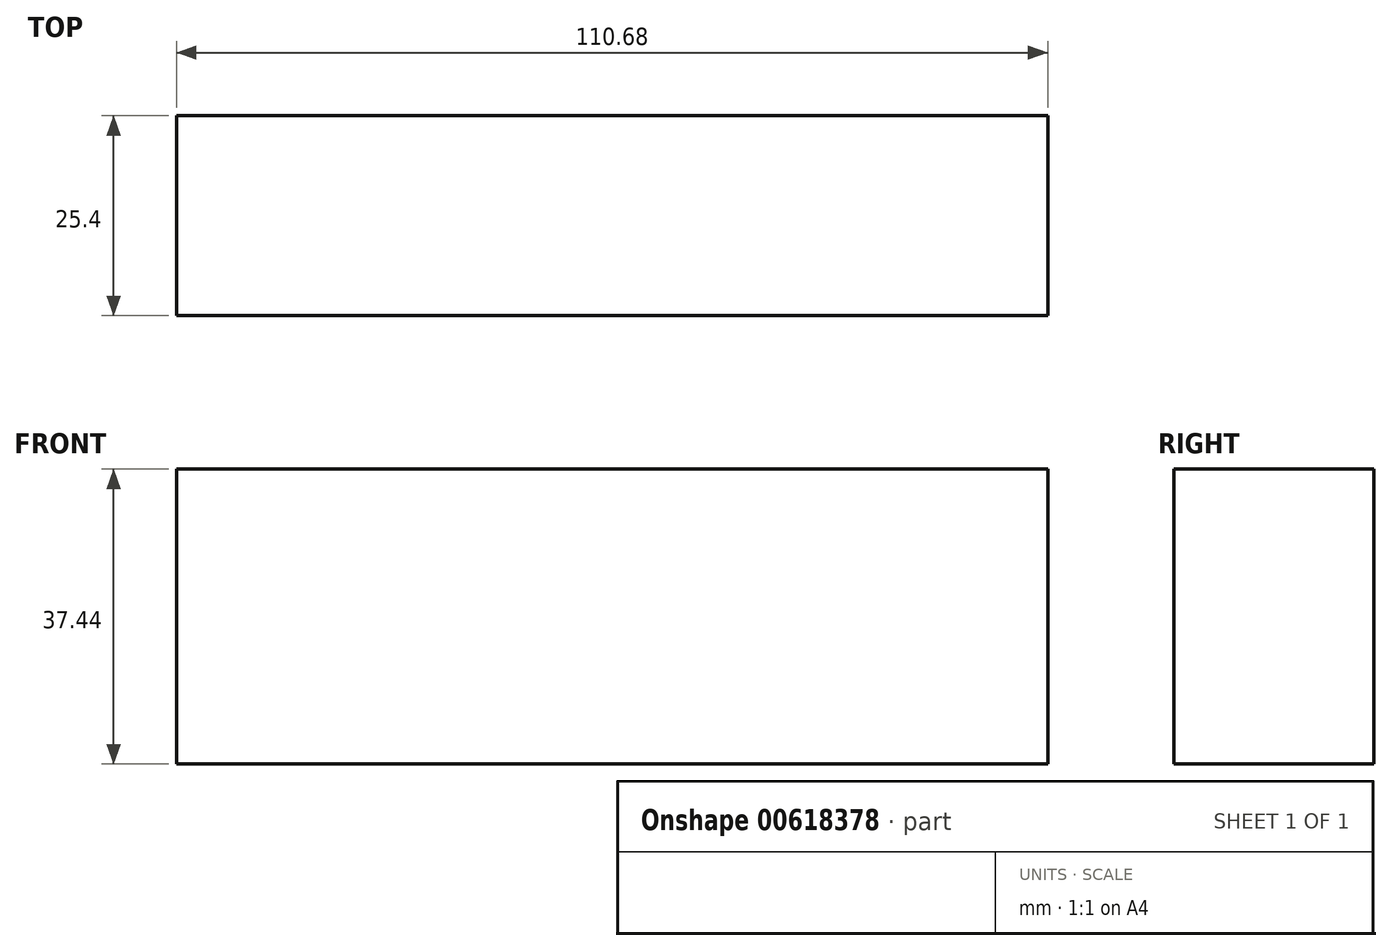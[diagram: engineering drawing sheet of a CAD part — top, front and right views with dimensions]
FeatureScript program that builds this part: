
annotation { "Feature Type Name" : "Feature", "Feature Type Description" : "" }
export const myFeature = defineFeature(function(context is Context, id is Id, definition is map)
    precondition{}
    {
        {
            var Q0;
            Q0=qCreatedBy(makeId("Top.planeOp"),FACE);
            var sketch = newSketch(context, id + "F0", { "sketchPlane" : qUnion([Q0])});
            skLineSegment(sketch, "E0", {"start": v(60.34, 47.6) * mm, "end": v(-50.34, 47.6) * mm});
            skLineSegment(sketch, "E1", {"start": v(-50.34, 47.6) * mm, "end": v(-50.34, -47.62) * mm});
            skLineSegment(sketch, "E2", {"start": v(-50.34, -47.62) * mm, "end": v(52.42, -47.62) * mm});
            skLineSegment(sketch, "E3", {"start": v(52.42, -47.62) * mm, "end": v(60.34, 47.6) * mm});
            skSolve(sketch);
        }
        {
            var Q0;
            Q0=makeQuery(id+"F0.imprint","IMPRINT",FACE,{"disambiguationData":[TD([[makeQuery(id+"F0.imprint","IMPRINT",EDGE,{"derivedFrom":sQuery(id+"F0.wireOp",EDGE,"E0")}),1.0]])]});
            var Q1;
            Q1=sQuery(id+"F0.wireOp",EDGE,"E2");
            var Q2;
            Q2=sQuery(id+"F0.wireOp",EDGE,"E3");
            var Q3;
            Q3=sQuery(id+"F0.wireOp",EDGE,"E0");
            extrude(context, id + "F1", {"entities" : qUnion([Q0]), "bodyType" : ToolBodyType.SURFACE, "surfaceEntities" : qUnion([Q1, Q2, Q3]), "depth" : 37.44 * mm, "offsetDistance" : 25.4 * mm});
        }
        {
            var Q0;
            Q0=makeQuery(id+"F1.opExtrude","SWEPT_FACE",FACE,{"disambiguationData":[OSD([sQuery(id+"F0.wireOp",EDGE,"E0")])]});
            extrude(context, id + "F2", {"entities" : qUnion([Q0]), "depth" : 25.4 * mm, "offsetDistance" : 25.4 * mm});
        }
    });
